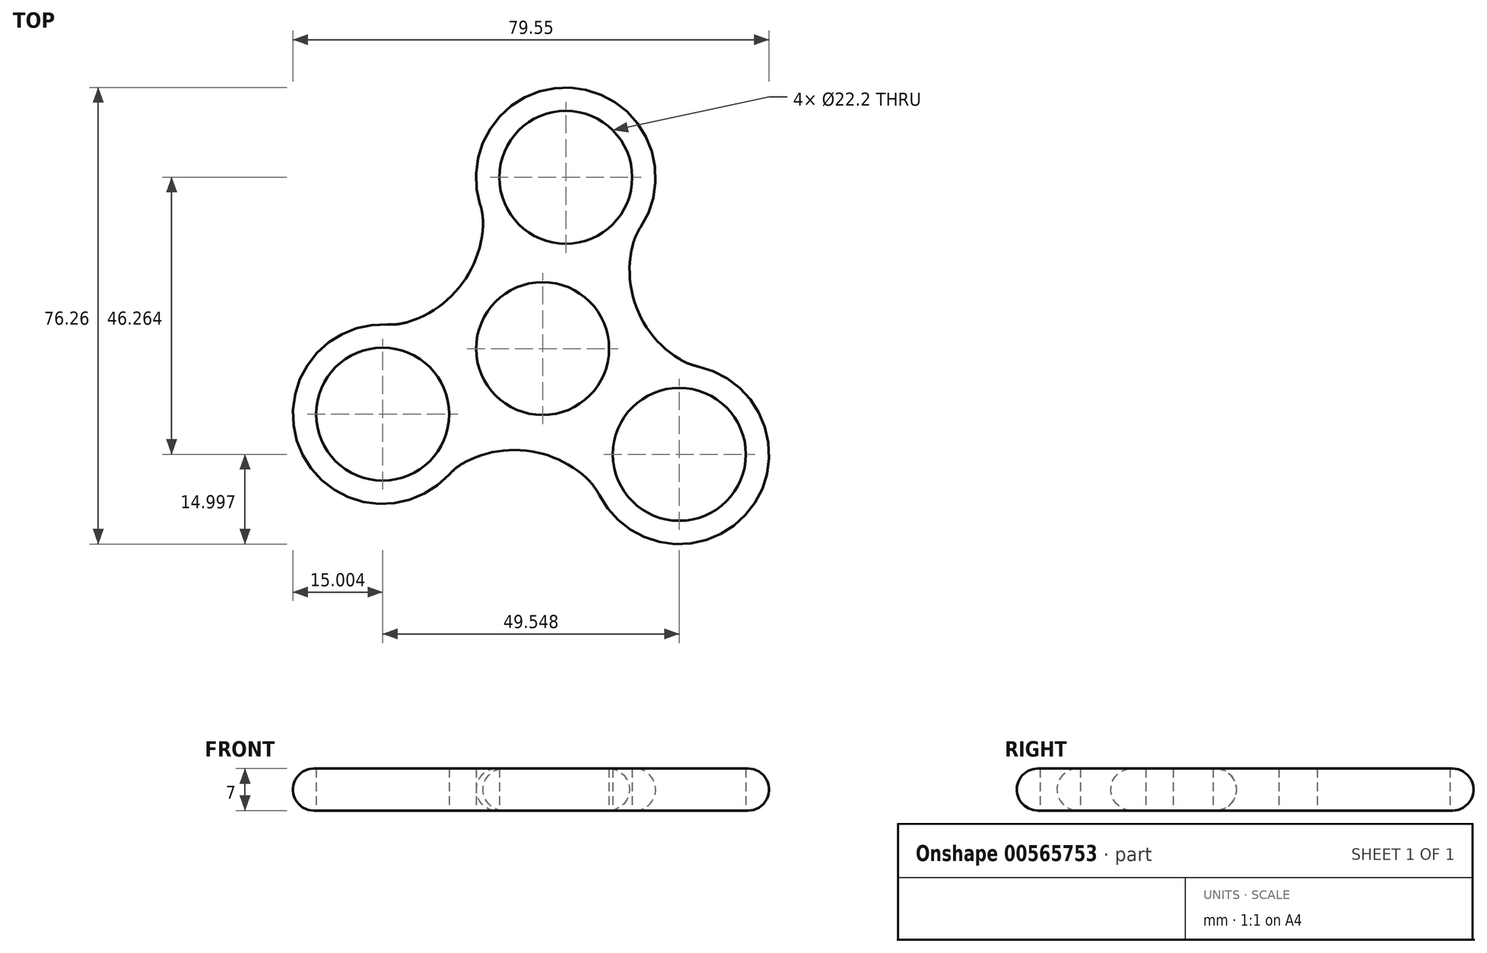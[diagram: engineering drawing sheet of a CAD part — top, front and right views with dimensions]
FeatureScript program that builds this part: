
annotation { "Feature Type Name" : "Feature", "Feature Type Description" : "" }
export const myFeature = defineFeature(function(context is Context, id is Id, definition is map)
    precondition{}
    {
        {
            var Q0;
            Q0=qCreatedBy(makeId("Top.planeOp"),FACE);
            var sketch = newSketch(context, id + "F0", { "sketchPlane" : qUnion([Q0])});
            skCircle(sketch, "E0", {"center": v(-2.06, 22.06) * mm, "radius": 11.1 * mm});
            skPoint(sketch, "E0.first.point", {"position": v(-13.1, 20.82) * mm});
            skPoint(sketch, "E0.second.point", {"position": v(8.98, 23.24) * mm});
            skPoint(sketch, "E0.third.point", {"position": v(1.39, 11.51) * mm});
            skCircle(sketch, "E1", {"center": v(-32.65, -17.5) * mm, "radius": 11.1 * mm});
            skCircle(sketch, "E2", {"center": v(16.9, -24.2) * mm, "radius": 11.1 * mm});
            skCircle(sketch, "E3", {"center": v(-5.94, -6.55) * mm, "radius": 11.1 * mm});
            skPoint(sketch, "E4.start.orphan", {"position": v(7.42, -1.07) * mm});
            skPoint(sketch, "E5.start.orphan", {"position": v(-17.35, 2.28) * mm});
            skPoint(sketch, "E6.start.orphan", {"position": v(-7.87, -20.85) * mm});
            skArc(sketch, "E7", {"start": v(-30.63, -2.63) * mm, "mid": v(-46.52, -23.18) * mm, "end": v(-20.78, -26.67) * mm});
            skArc(sketch, "E8", {"start": v(9.8, 12.89) * mm, "mid": v(-0.05, 36.93) * mm, "end": v(-15.94, 16.37) * mm});
            skArc(sketch, "E9", {"start": v(3.02, -29.9) * mm, "mid": v(28.77, -33.38) * mm, "end": v(18.91, -9.34) * mm});
            skArc(sketch, "E10", {"start": v(-30.63, -2.63) * mm, "mid": v(-19.58, 4) * mm, "end": v(-15.94, 16.37) * mm});
            skArc(sketch, "E11", {"start": v(9.8, 12.89) * mm, "mid": v(9.89, -0.06) * mm, "end": v(18.91, -9.34) * mm});
            skArc(sketch, "E12", {"start": v(3.02, -29.9) * mm, "mid": v(-8.25, -23.64) * mm, "end": v(-20.78, -26.67) * mm});
            skSolve(sketch);
        }
        {
            var Q0;
            Q0 = qSketchRegion(id + "F0", true);
            extrude(context, id + "F1", {"entities" : qUnion([Q0]), "depth" : 7 * mm, "offsetDistance" : 25 * mm});
        }
        {
            var Q0;
            Q0=makeQuery(id+"F1.opExtrude","SWEPT_EDGE",EDGE,{"disambiguationData":[OSD([sQuery(id+"F0.wireOp",EDGE,"E9"),sQuery(id+"F0.wireOp",EDGE,"E11")])]});
            var Q1;
            Q1=makeQuery(id+"F1.opExtrude","SWEPT_EDGE",EDGE,{"disambiguationData":[OSD([sQuery(id+"F0.wireOp",EDGE,"E8"),sQuery(id+"F0.wireOp",EDGE,"E11")])]});
            var Q2;
            Q2=makeQuery(id+"F1.opExtrude","SWEPT_EDGE",EDGE,{"disambiguationData":[OSD([sQuery(id+"F0.wireOp",EDGE,"E8"),sQuery(id+"F0.wireOp",EDGE,"E10")])]});
            var Q3;
            Q3=makeQuery(id+"F1.opExtrude","SWEPT_EDGE",EDGE,{"disambiguationData":[OSD([sQuery(id+"F0.wireOp",EDGE,"E7"),sQuery(id+"F0.wireOp",EDGE,"E10")])]});
            var Q4;
            Q4=makeQuery(id+"F1.opExtrude","SWEPT_EDGE",EDGE,{"disambiguationData":[OSD([sQuery(id+"F0.wireOp",EDGE,"E7"),sQuery(id+"F0.wireOp",EDGE,"E12")])]});
            var Q5;
            Q5=makeQuery(id+"F1.opExtrude","SWEPT_EDGE",EDGE,{"disambiguationData":[OSD([sQuery(id+"F0.wireOp",EDGE,"E9"),sQuery(id+"F0.wireOp",EDGE,"E12")])]});
            fillet(context, id + "F2", {"entities" : qUnion([Q0, Q1, Q2, Q3, Q4, Q5]), "radius" : 10 * mm, "tangentPropagation" : true, "allowEdgeOverflow" : false});
        }
        {
            var Q0;
            Q0=makeQuery(id+"F1.opExtrude","CAP_EDGE",EDGE,{"disambiguationData":[OSD([sQuery(id+"F0.wireOp",EDGE,"E12")])],"isStart":false});
            fillet(context, id + "F3", {"entities" : qUnion([Q0]), "radius" : 3.5 * mm, "tangentPropagation" : true, "allowEdgeOverflow" : false});
        }
        {
            var Q0;
            Q0=makeQuery(id+"F1.opExtrude","CAP_EDGE",EDGE,{"disambiguationData":[OSD([sQuery(id+"F0.wireOp",EDGE,"E7")])],"isStart":true});
            fillet(context, id + "F4", {"entities" : qUnion([Q0]), "radius" : 3.5 * mm, "tangentPropagation" : true, "allowEdgeOverflow" : false});
        }
    });
